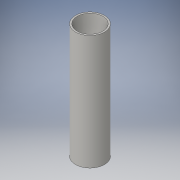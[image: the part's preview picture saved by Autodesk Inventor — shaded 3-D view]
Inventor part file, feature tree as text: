
AUTODESK INVENTOR PART (.ipt)
format: ipt  version: 2016 (Build 200138000, 138)  size: 93,184 bytes
history: native  units: in
note: dims shown in document units (in); Inventor stores cm internally (conversion verified against a paired STEP export)
features: sketch x2, extrude x1
ambient origin geometry x8: Origin, YZ Plane, XZ Plane, XY Plane, X Axis, Y Axis, Z Axis, Center Point
bodies: Solid1 (feature_tree)
feature tree (3):
  extrude  "Extrusion1"  Depth=3.994in
  sketch  "Sketch2"  dims[d2=17.814in d3=0.0in]
  sketch  "Sketch1"  dims[d0=4.496in d1=3.994in]
